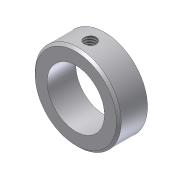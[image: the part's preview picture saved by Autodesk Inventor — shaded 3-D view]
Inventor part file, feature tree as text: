
AUTODESK INVENTOR PART (.ipt)
format: ipt  version: unknown  size: 184,832 bytes
history: native  units: mm (DEFAULTED — no unit token found)
features: sketch x2, extrude x1, chamfer x1, hole x1
ambient origin geometry x8: Origin, YZ Plane, XZ Plane, XY Plane, X Axis, Y Axis, Z Axis, Center Point
feature tree (5):
  extrude  "Extrusion1"  Depth=19.05mm
  chamfer  "Chamfer1"  Distance=9.525mm
  hole  "Hole1"  [1 undecoded]
  sketch  "Sketch1"  dims[d0=28.575mm d1=19.05mm d2=9.525mm d3=0.0mm]
  sketch  "Sketch3"  dims[d4=0.7874mm d5=3.175mm d8=4.7625mm d9=3.9624mm d10=12.7mm d11=9.525mm d12=6.35mm d13=14.3117mm d14=19.05mm d15=20.594885mm d16=45.0deg]
note: 1 required parameter value undecoded (feature->parameter linkage not recoverable at this tier; creation-order binding heuristic only, values carry confidence <= 0.55)
